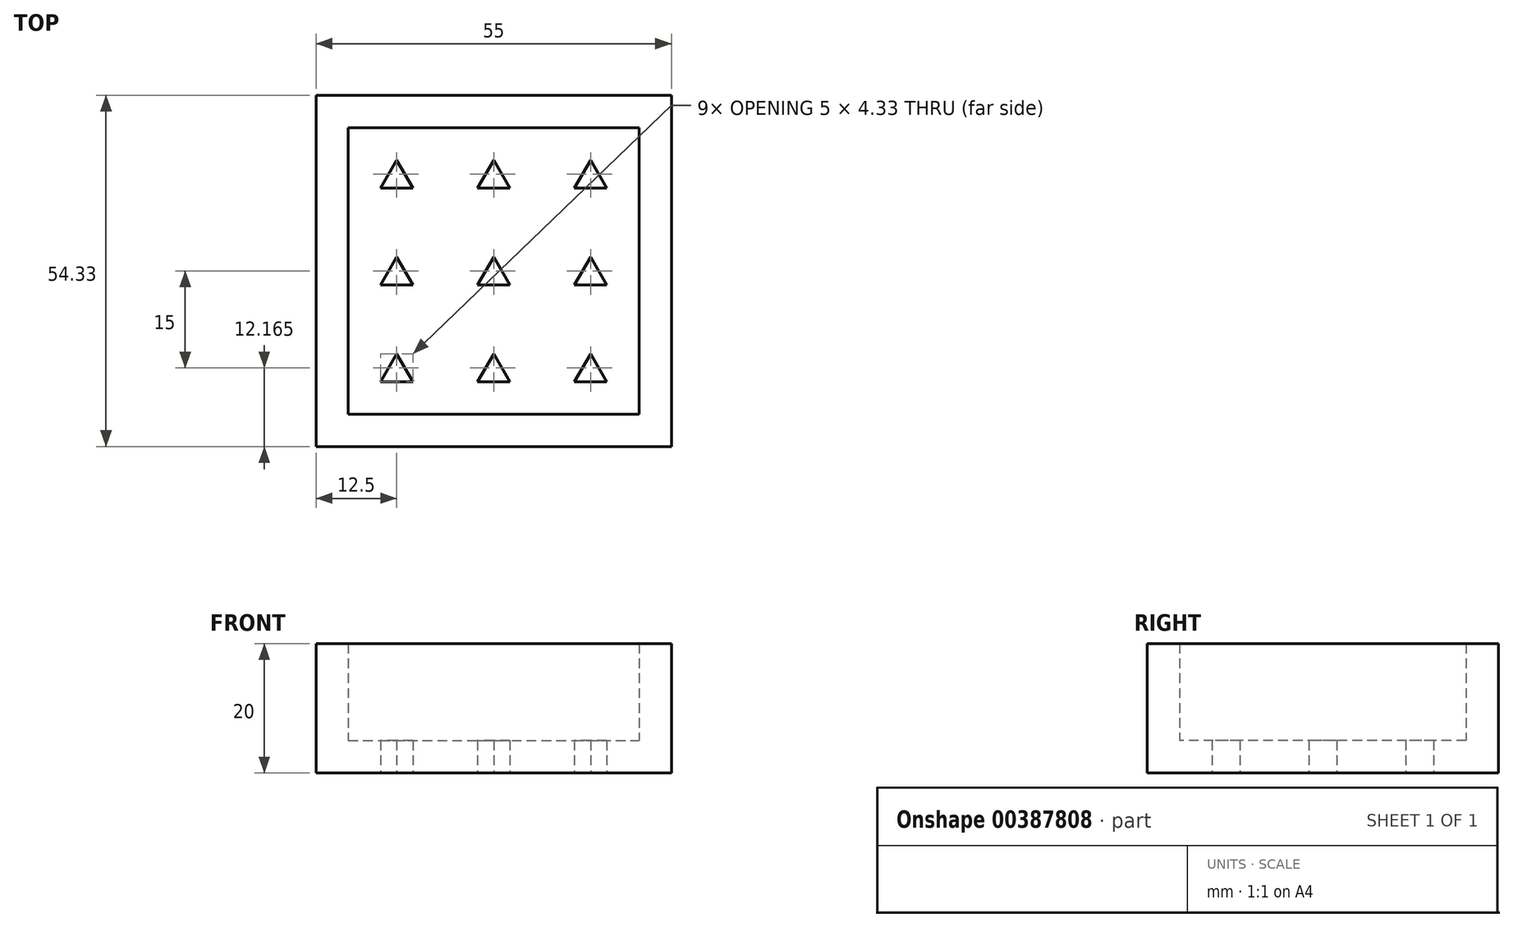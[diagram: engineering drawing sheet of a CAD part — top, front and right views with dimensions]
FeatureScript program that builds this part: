
annotation { "Feature Type Name" : "Feature", "Feature Type Description" : "" }
export const myFeature = defineFeature(function(context is Context, id is Id, definition is map)
    precondition{}
    {
        {
            var Q0;
            Q0=qCreatedBy(makeId("Top.planeOp"),FACE);
            var sketch = newSketch(context, id + "F0", { "sketchPlane" : qUnion([Q0])});
            skLineSegment(sketch, "E0", {"start": v(-2.5, 4.33) * mm, "end": v(-5, 0) * mm});
            skLineSegment(sketch, "E1", {"start": v(0, 0) * mm, "end": v(-2.5, 4.33) * mm});
            skLineSegment(sketch, "E2", {"start": v(-5, 0) * mm, "end": v(0, 0) * mm});
            skLineSegment(sketch, "E3.0.1.0", {"start": v(-5, 15) * mm, "end": v(0, 15) * mm});
            skLineSegment(sketch, "E3.0.1.1", {"start": v(0, 15) * mm, "end": v(-2.5, 19.33) * mm});
            skLineSegment(sketch, "E3.0.1.2", {"start": v(-2.5, 19.33) * mm, "end": v(-5, 15) * mm});
            skLineSegment(sketch, "E3.0.2.0", {"start": v(-5, 30) * mm, "end": v(0, 30) * mm});
            skLineSegment(sketch, "E3.0.2.1", {"start": v(0, 30) * mm, "end": v(-2.5, 34.33) * mm});
            skLineSegment(sketch, "E3.0.2.2", {"start": v(-2.5, 34.33) * mm, "end": v(-5, 30) * mm});
            skLineSegment(sketch, "E3.1.0.0", {"start": v(10, 0) * mm, "end": v(15, 0) * mm});
            skLineSegment(sketch, "E3.1.0.1", {"start": v(15, 0) * mm, "end": v(12.5, 4.33) * mm});
            skLineSegment(sketch, "E3.1.0.2", {"start": v(12.5, 4.33) * mm, "end": v(10, 0) * mm});
            skLineSegment(sketch, "E3.1.1.0", {"start": v(10, 15) * mm, "end": v(15, 15) * mm});
            skLineSegment(sketch, "E3.1.1.1", {"start": v(15, 15) * mm, "end": v(12.5, 19.33) * mm});
            skLineSegment(sketch, "E3.1.1.2", {"start": v(12.5, 19.33) * mm, "end": v(10, 15) * mm});
            skLineSegment(sketch, "E3.1.2.0", {"start": v(10, 30) * mm, "end": v(15, 30) * mm});
            skLineSegment(sketch, "E3.1.2.1", {"start": v(15, 30) * mm, "end": v(12.5, 34.33) * mm});
            skLineSegment(sketch, "E3.1.2.2", {"start": v(12.5, 34.33) * mm, "end": v(10, 30) * mm});
            skLineSegment(sketch, "E3.2.0.0", {"start": v(25, 0) * mm, "end": v(30, 0) * mm});
            skLineSegment(sketch, "E3.2.0.1", {"start": v(30, 0) * mm, "end": v(27.5, 4.33) * mm});
            skLineSegment(sketch, "E3.2.0.2", {"start": v(27.5, 4.33) * mm, "end": v(25, 0) * mm});
            skLineSegment(sketch, "E3.2.1.0", {"start": v(25, 15) * mm, "end": v(30, 15) * mm});
            skLineSegment(sketch, "E3.2.1.1", {"start": v(30, 15) * mm, "end": v(27.5, 19.33) * mm});
            skLineSegment(sketch, "E3.2.1.2", {"start": v(27.5, 19.33) * mm, "end": v(25, 15) * mm});
            skLineSegment(sketch, "E3.2.2.0", {"start": v(25, 30) * mm, "end": v(30, 30) * mm});
            skLineSegment(sketch, "E3.2.2.1", {"start": v(30, 30) * mm, "end": v(27.5, 34.33) * mm});
            skLineSegment(sketch, "E3.2.2.2", {"start": v(27.5, 34.33) * mm, "end": v(25, 30) * mm});
            skLineSegment(sketch, "E3.direction1", {"start": v(-5, 0) * mm, "end": v(10, 0) * mm, "construction": true});
            skLineSegment(sketch, "E3.direction2", {"start": v(-5, 0) * mm, "end": v(-5, 15) * mm, "construction": true});
            skLineSegment(sketch, "E4.bottom", {"start": v(-15, 44.33) * mm, "end": v(40, 44.33) * mm});
            skLineSegment(sketch, "E4.top", {"start": v(-15, -10) * mm, "end": v(40, -10) * mm});
            skLineSegment(sketch, "E4.left", {"start": v(-15, 44.33) * mm, "end": v(-15, -10) * mm});
            skLineSegment(sketch, "E4.right", {"start": v(40, 44.33) * mm, "end": v(40, -10) * mm});
            skSolve(sketch);
        }
        {
            var Q0;
            Q0=makeQuery(id+"F0.imprint","IMPRINT",FACE,{"disambiguationData":[TD([[makeQuery(id+"F0.imprint","IMPRINT",EDGE,{"derivedFrom":sQuery(id+"F0.wireOp",EDGE,"E0")}),-1.0]])]});
            extrude(context, id + "F1", {"entities" : qUnion([Q0]), "depth" : 5 * mm});
        }
        {
            var Q0;
            Q0=makeQuery(id+"F1.opExtrude","CAP_FACE",FACE,{"disambiguationData":[OSD([sQuery(id+"F0.wireOp",EDGE,"E0"),sQuery(id+"F0.wireOp",EDGE,"E1"),sQuery(id+"F0.wireOp",EDGE,"E2"),sQuery(id+"F0.wireOp",EDGE,"E3.0.1.0"),sQuery(id+"F0.wireOp",EDGE,"E3.0.1.1"),sQuery(id+"F0.wireOp",EDGE,"E3.0.1.2"),sQuery(id+"F0.wireOp",EDGE,"E3.0.2.0"),sQuery(id+"F0.wireOp",EDGE,"E3.0.2.1"),sQuery(id+"F0.wireOp",EDGE,"E3.0.2.2"),sQuery(id+"F0.wireOp",EDGE,"E3.1.0.0"),sQuery(id+"F0.wireOp",EDGE,"E3.1.0.1"),sQuery(id+"F0.wireOp",EDGE,"E3.1.0.2"),sQuery(id+"F0.wireOp",EDGE,"E3.1.1.0"),sQuery(id+"F0.wireOp",EDGE,"E3.1.1.1"),sQuery(id+"F0.wireOp",EDGE,"E3.1.1.2"),sQuery(id+"F0.wireOp",EDGE,"E3.1.2.0"),sQuery(id+"F0.wireOp",EDGE,"E3.1.2.1"),sQuery(id+"F0.wireOp",EDGE,"E3.1.2.2"),sQuery(id+"F0.wireOp",EDGE,"E3.2.0.0"),sQuery(id+"F0.wireOp",EDGE,"E3.2.0.1"),sQuery(id+"F0.wireOp",EDGE,"E3.2.0.2"),sQuery(id+"F0.wireOp",EDGE,"E3.2.1.0"),sQuery(id+"F0.wireOp",EDGE,"E3.2.1.1"),sQuery(id+"F0.wireOp",EDGE,"E3.2.1.2"),sQuery(id+"F0.wireOp",EDGE,"E3.2.2.0"),sQuery(id+"F0.wireOp",EDGE,"E3.2.2.1"),sQuery(id+"F0.wireOp",EDGE,"E3.2.2.2"),sQuery(id+"F0.wireOp",EDGE,"E4.bottom"),sQuery(id+"F0.wireOp",EDGE,"E4.top"),sQuery(id+"F0.wireOp",EDGE,"E4.left"),sQuery(id+"F0.wireOp",EDGE,"E4.right")])],"isStart":false});
            var sketch = newSketch(context, id + "F2", { "sketchPlane" : qUnion([Q0])});
            skLineSegment(sketch, "E5.0", {"start": v(-10, 39.33) * mm, "end": v(-10, -5) * mm});
            skLineSegment(sketch, "E5.1", {"start": v(35, 39.33) * mm, "end": v(-10, 39.33) * mm});
            skLineSegment(sketch, "E5.2", {"start": v(35, -5) * mm, "end": v(35, 39.33) * mm});
            skLineSegment(sketch, "E5.3", {"start": v(-10, -5) * mm, "end": v(35, -5) * mm});
            skSolve(sketch);
        }
        {
            var Q0;
            Q0=makeQuery(id+"F2.imprint","IMPRINT",FACE,{"disambiguationData":[TD([[makeQuery(id+"F2.imprint","IMPRINT",EDGE,{"derivedFrom":sQuery(id+"F2.wireOp",EDGE,"E5.0")}),-1.0]])]});
            extrude(context, id + "F3", {"entities" : qUnion([Q0]), "operationType" : NewBodyOperationType.ADD, "depth" : 15 * mm});
        }
    });
